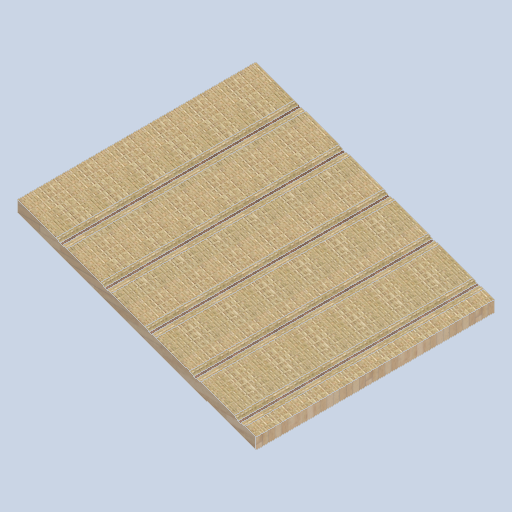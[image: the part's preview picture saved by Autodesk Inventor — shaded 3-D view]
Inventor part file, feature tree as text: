
AUTODESK INVENTOR PART (.ipt)
format: ipt  version: 2024.2 (Build 282272000, 272)  size: 356,352 bytes
history: native  units: in
note: dims shown in document units (in); Inventor stores cm internally (conversion verified against a paired STEP export)
features: other x3, sketch x3, plane x3
ambient origin geometry x8: Origin, YZ Plane, XZ Plane, XY Plane, X Axis, Y Axis, Z Axis, Center Point
bodies: Solid1 (feature_tree)
feature tree (9):
  other  "side_curve_panel_01.ipt"
  other  "Solid1::side_curve_panel_01.ipt"
  other  "TaggingFeature1"
  sketch  "Sketch1"  dims[d0=0.3937in]
  sketch  "Sketch4"
  sketch  "Sketch5"
  plane  "Work Plane1"
  plane  "Work Plane2"
  plane  "Work Plane3"
